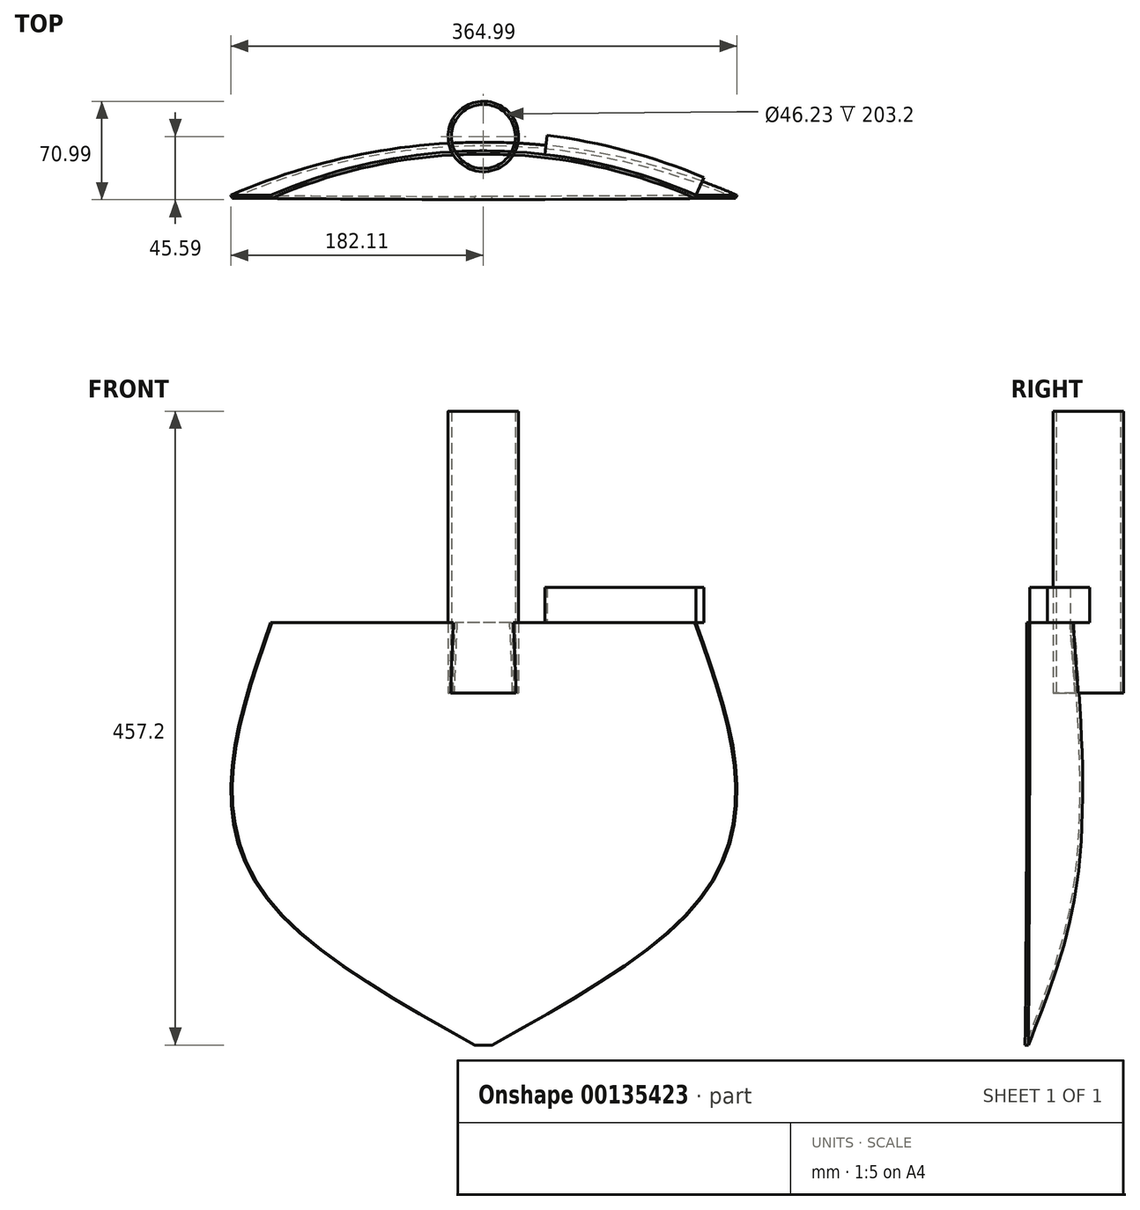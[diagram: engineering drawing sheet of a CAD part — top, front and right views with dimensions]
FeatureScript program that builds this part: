
annotation { "Feature Type Name" : "Feature", "Feature Type Description" : "" }
export const myFeature = defineFeature(function(context is Context, id is Id, definition is map)
    precondition{}
    {
        {
            var Q0;
            Q0=qCreatedBy(makeId("Top.planeOp"),FACE);
            var sketch = newSketch(context, id + "F0", { "sketchPlane" : qUnion([Q0])});
            skCircle(sketch, "E0", {"center": v(0, 0) * mm, "radius": 25.4 * mm});
            skCircle(sketch, "E1.0", {"center": v(0, 0) * mm, "radius": 23.11 * mm});
            skSolve(sketch);
        }
        {
            var Q0;
            Q0 = qSketchRegion(id + "F0", true);
            extrude(context, id + "F1", {"entities" : qUnion([Q0]), "depth" : 152.4 * mm, "hasSecondDirection" : true, "secondDirectionOppositeDirection" : true, "secondDirectionDepth" : 50.8 * mm});
        }
        {
            var Q0;
            Q0=qCreatedBy(makeId("Top.planeOp"),FACE);
            var sketch = newSketch(context, id + "F2", { "sketchPlane" : qUnion([Q0])});
            skLineSegment(sketch, "E2", {"start": v(-152.4, -44.45) * mm, "end": v(152.4, -44.45) * mm, "construction": true});
            skLineSegment(sketch, "E3", {"start": v(0, 0) * mm, "end": v(0, -44.45) * mm, "construction": true});
            skArc(sketch, "E4", {"start": v(152.4, -44.45) * mm, "mid": v(0, -12.7) * mm, "end": v(-152.4, -44.45) * mm});
            skArc(sketch, "E5.0", {"start": v(153.31, -42.35) * mm, "mid": v(0, -10.41) * mm, "end": v(-153.31, -42.35) * mm});
            skLineSegment(sketch, "E6", {"start": v(-153.31, -42.35) * mm, "end": v(-152.4, -44.45) * mm});
            skLineSegment(sketch, "E7", {"start": v(152.4, -44.45) * mm, "end": v(153.31, -42.35) * mm});
            skLineSegment(sketch, "E8", {"start": v(152.4, -44.45) * mm, "end": v(162.59, -48.89) * mm, "construction": true});
            skLineSegment(sketch, "E9", {"start": v(-152.4, -44.45) * mm, "end": v(-160.79, -48.1) * mm, "construction": true});
            skSolve(sketch);
        }
        {
            var Q0;
            Q0=qCreatedBy(makeId("Top.planeOp"),FACE);
            cPlane(context, id + "F3", {"entities" : qUnion([Q0]), "cplaneType" : CPlaneType.OFFSET, "offset" : 304.8 * mm, "oppositeDirection" : true, "width" : 152.4 * mm, "height" : 152.4 * mm});
        }
        {
            var Q0;
            Q0=qCreatedBy(id+"F3.planeOp",FACE);
            var sketch = newSketch(context, id + "F4", { "sketchPlane" : qUnion([Q0])});
            skLineSegment(sketch, "E10.bottom", {"start": v(6.25, -45.6) * mm, "end": v(-6.25, -45.6) * mm});
            skLineSegment(sketch, "E10.top", {"start": v(6.25, -43.3) * mm, "end": v(-6.25, -43.3) * mm});
            skLineSegment(sketch, "E10.left", {"start": v(6.25, -45.6) * mm, "end": v(6.25, -43.3) * mm});
            skLineSegment(sketch, "E10.right", {"start": v(-6.25, -45.6) * mm, "end": v(-6.25, -43.3) * mm});
            skPoint(sketch, "E10.middle", {"position": v(0, -44.45) * mm});
            skSolve(sketch);
        }
        {
            var Q0;
            Q0=qCreatedBy(makeId("Top.planeOp"),FACE);
            cPlane(context, id + "F5", {"entities" : qUnion([Q0]), "cplaneType" : CPlaneType.OFFSET, "offset" : 203.2 * mm, "oppositeDirection" : true, "width" : 152.4 * mm, "height" : 152.4 * mm});
        }
        {
            var Q0;
            Q0=qCreatedBy(id+"F5.planeOp",FACE);
            var sketch = newSketch(context, id + "F6", { "sketchPlane" : qUnion([Q0])});
            skArc(sketch, "E11", {"start": v(152.83, -44.72) * mm, "mid": v(0.43, -12.97) * mm, "end": v(-151.97, -44.72) * mm});
            skArc(sketch, "E12.0", {"start": v(153.74, -42.62) * mm, "mid": v(0.43, -10.68) * mm, "end": v(-152.88, -42.62) * mm});
            skLineSegment(sketch, "E13", {"start": v(-152.88, -42.62) * mm, "end": v(-151.97, -44.72) * mm});
            skLineSegment(sketch, "E14", {"start": v(152.83, -44.72) * mm, "end": v(153.74, -42.62) * mm});
            skSolve(sketch);
        }
        {
            var Q1;
            Q1=makeQuery(id+"F2.imprint","IMPRINT",FACE,{"disambiguationData":[TD([[makeQuery(id+"F2.imprint","IMPRINT",EDGE,{"derivedFrom":sQuery(id+"F2.wireOp",EDGE,"E4")}),-1.0]])]});
            var Q2;
            Q2=makeQuery(id+"F6.imprint","IMPRINT",FACE,{"disambiguationData":[TD([[makeQuery(id+"F6.imprint","IMPRINT",EDGE,{"derivedFrom":sQuery(id+"F6.wireOp",EDGE,"E11")}),-1.0]])]});
            var Q3;
            Q3=makeQuery(id+"F4.imprint","IMPRINT",FACE,{"disambiguationData":[TD([[makeQuery(id+"F4.imprint","IMPRINT",EDGE,{"derivedFrom":sQuery(id+"F4.wireOp",EDGE,"E10.bottom")}),-1.0]])]});
            loft(context, id + "F7", {"operationType" : NewBodyOperationType.ADD, "sheetProfilesArray" : [{ "sheetProfileEntities" : qUnion([Q1]) }, { "sheetProfileEntities" : qUnion([Q2]) }, { "sheetProfileEntities" : qUnion([Q3]) }]});
        }
        {
            var Q0;
            {var subQ0=sQuery(id+"F6.wireOp",EDGE,"E14");var subQ2=sQuery(id+"F6.wireOp",EDGE,"E11");var subQ3=sQuery(id+"F2.wireOp",EDGE,"E7");var subQ5=sQuery(id+"F2.wireOp",EDGE,"E4");var subQ6=sQuery(id+"F6.wireOp",EDGE,"E12.0");var subQ7=sQuery(id+"F2.wireOp",EDGE,"E5.0");Q0=makeQuery(id+"F7.boolean.opBoolean","SPLIT",FACE,{"disambiguationData":[TD([makeQuery(id+"F7.opLoft","SWEPT_FACE",FACE,{"disambiguationData":[OSD([subQ5,subQ7,subQ3,subQ2,subQ6,subQ0])]})])],"derivedFrom":makeQuery(id+"F7.opLoft","CAP_FACE",FACE,{"disambiguationData":[OSD([makeQuery(id+"F2.imprint","IMPRINT",FACE,{"disambiguationData":[TD([[makeQuery(id+"F2.imprint","IMPRINT",EDGE,{"derivedFrom":subQ5}),-1.0]])]})])],"isStart":true})});}
            var sketch = newSketch(context, id + "F8", { "sketchPlane" : qUnion([Q0])});
            skLineSegment(sketch, "E15", {"start": v(152.4, -44.45) * mm, "end": v(158.9, -29.52) * mm});
            skLineSegment(sketch, "E16", {"start": v(43.94, -15.24) * mm, "end": v(45.82, 0.94) * mm});
            skArc(sketch, "E17", {"start": v(158.9, -29.52) * mm, "mid": v(103.4, -10.44) * mm, "end": v(45.82, 0.94) * mm});
            skArc(sketch, "E18", {"start": v(152.4, -44.45) * mm, "mid": v(99.16, -26.16) * mm, "end": v(43.94, -15.24) * mm});
            skLineSegment(sketch, "E19", {"start": v(0, 0) * mm, "end": v(0, 15.36) * mm, "construction": true});
            skArc(sketch, "E20.MirrorCS", {"start": v(-158.9, -29.52) * mm, "mid": v(-103.4, -10.44) * mm, "end": v(-45.82, 0.94) * mm});
            skArc(sketch, "E21.MirrorCS", {"start": v(-152.4, -44.45) * mm, "mid": v(-99.16, -26.16) * mm, "end": v(-43.94, -15.24) * mm});
            skLineSegment(sketch, "E22.MirrorCS", {"start": v(-152.4, -44.45) * mm, "end": v(-158.9, -29.52) * mm});
            skLineSegment(sketch, "E23.MirrorCS", {"start": v(-43.94, -15.24) * mm, "end": v(-45.82, 0.94) * mm});
            skSolve(sketch);
        }
        {
            var Q0;
            {var subQ9=sQuery(id+"F8.wireOp",EDGE,"E17");Q0=makeQuery(id+"F8.imprint","IMPRINT",FACE,{"disambiguationData":[TD([[makeQuery(id+"F8.imprint","IMPRINT",EDGE,{"derivedFrom":subQ9}),1.0]])]});}
            var Q1;
            Q1=makeQuery(id+"F8.imprint","IMPRINT",FACE,{"disambiguationData":[TD([[makeQuery(id+"F8.imprint","IMPRINT",EDGE,{"derivedFrom":sQuery(id+"F8.wireOp",EDGE,"E20.MirrorCS")}),-1.0]])]});
            extrude(context, id + "F9", {"entities" : qUnion([Q0, Q1]), "operationType" : NewBodyOperationType.ADD, "depth" : 25.4 * mm});
        }
    });
